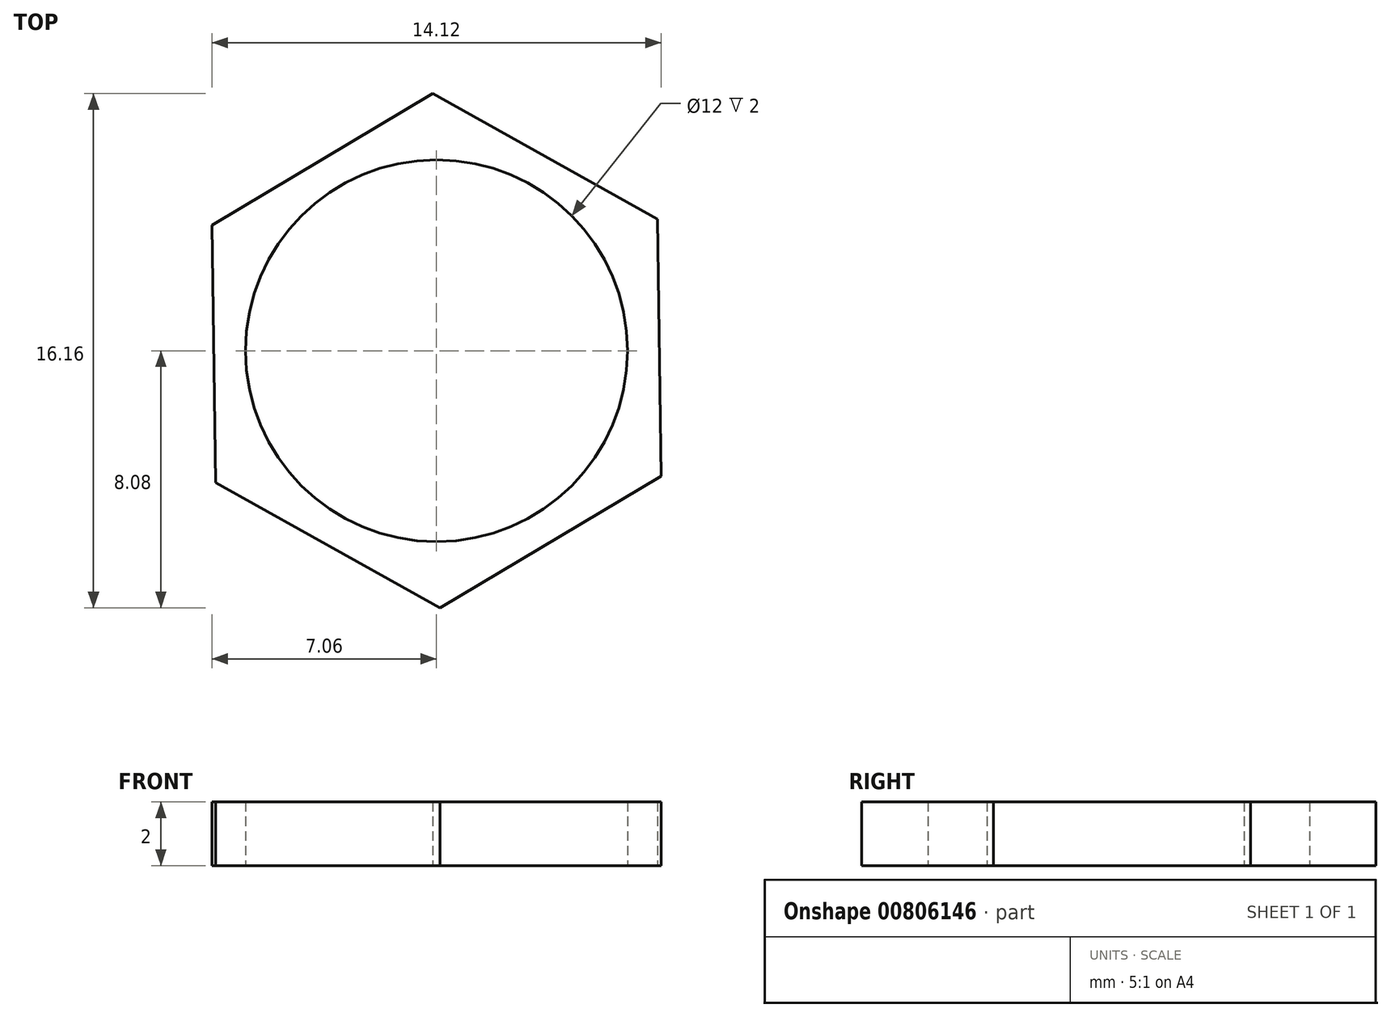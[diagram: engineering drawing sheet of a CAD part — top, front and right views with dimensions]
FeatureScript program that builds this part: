
annotation { "Feature Type Name" : "Feature", "Feature Type Description" : "" }
export const myFeature = defineFeature(function(context is Context, id is Id, definition is map)
    precondition{}
    {
        {
            var Q0;
            Q0=qCreatedBy(makeId("Top.planeOp"),FACE);
            var sketch = newSketch(context, id + "F0", { "sketchPlane" : qUnion([Q0])});
            skCircle(sketch, "E0.cCircle", {"center": v(0, 0) * mm, "radius": 7 * mm, "construction": true});
            skLineSegment(sketch, "E0.0", {"start": v(0.11, -8.08) * mm, "end": v(-6.94, -4.14) * mm});
            skLineSegment(sketch, "E0.1", {"start": v(-6.94, -4.14) * mm, "end": v(-7.06, 3.94) * mm});
            skLineSegment(sketch, "E0.2", {"start": v(-7.06, 3.94) * mm, "end": v(-0.11, 8.08) * mm});
            skLineSegment(sketch, "E0.3", {"start": v(-0.11, 8.08) * mm, "end": v(6.94, 4.14) * mm});
            skLineSegment(sketch, "E0.4", {"start": v(6.94, 4.14) * mm, "end": v(7.06, -3.94) * mm});
            skLineSegment(sketch, "E0.5", {"start": v(7.06, -3.94) * mm, "end": v(0.11, -8.08) * mm});
            skPoint(sketch, "E0.0.midPoint", {"position": v(-3.41, -6.11) * mm});
            skCircle(sketch, "E1", {"center": v(0, 0) * mm, "radius": 6 * mm});
            skSolve(sketch);
        }
        {
            var Q0;
            Q0 = qSketchRegion(id + "F0", true);
            extrude(context, id + "F1", {"entities" : qUnion([Q0]), "depth" : 2 * mm, "offsetDistance" : 25.4 * mm});
        }
    });
